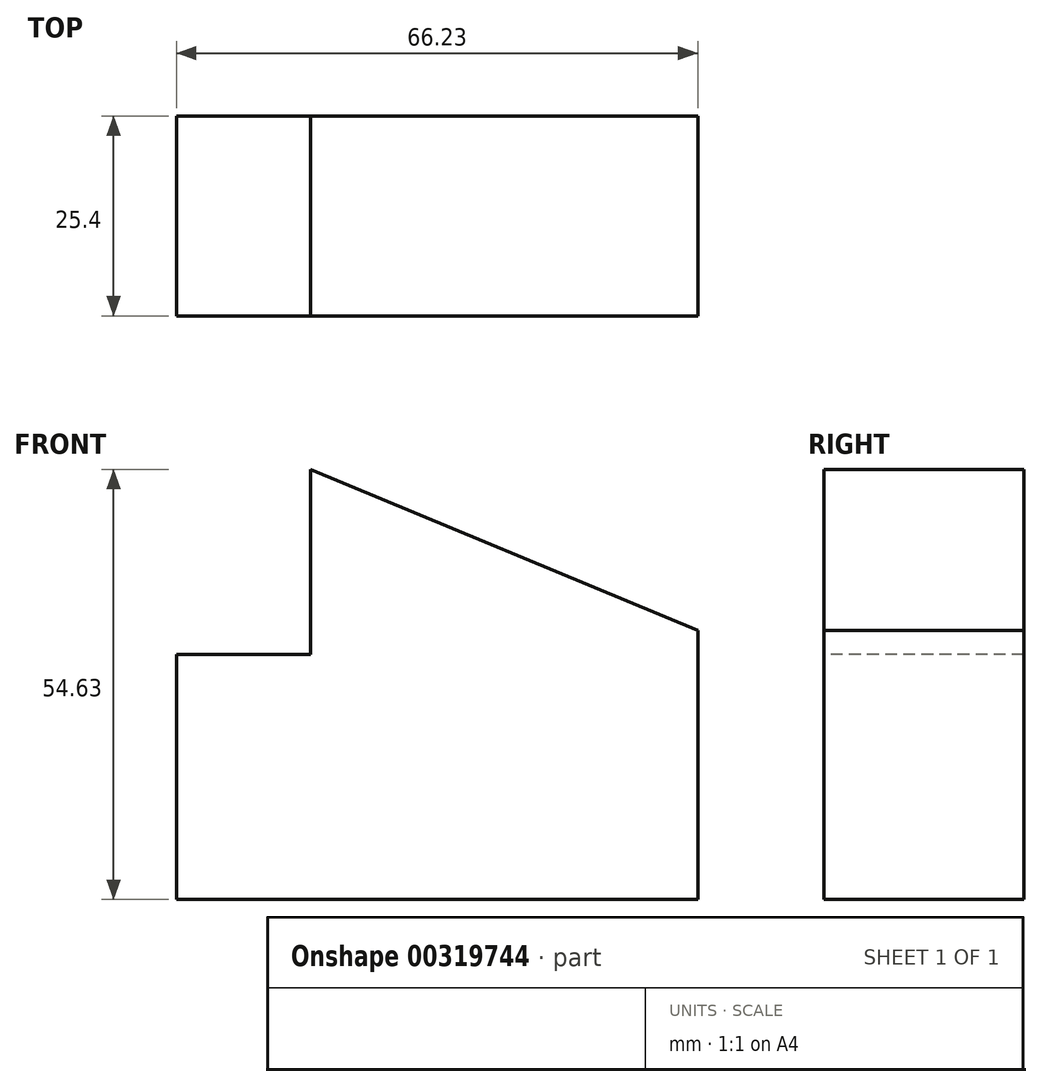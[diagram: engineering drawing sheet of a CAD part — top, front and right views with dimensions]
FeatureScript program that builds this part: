
annotation { "Feature Type Name" : "Feature", "Feature Type Description" : "" }
export const myFeature = defineFeature(function(context is Context, id is Id, definition is map)
    precondition{}
    {
        {
            var Q0;
            Q0=qCreatedBy(makeId("Front.planeOp"),FACE);
            var sketch = newSketch(context, id + "F0", { "sketchPlane" : qUnion([Q0])});
            skLineSegment(sketch, "E0", {"start": v(-19.5, 45.34) * mm, "end": v(-19.5, 31.1) * mm});
            skLineSegment(sketch, "E1", {"start": v(-19.5, 31.1) * mm, "end": v(-36.52, 31.1) * mm});
            skLineSegment(sketch, "E2", {"start": v(-36.52, 31.1) * mm, "end": v(-36.52, 0) * mm});
            skLineSegment(sketch, "E3", {"start": v(-36.52, 0) * mm, "end": v(29.71, 0) * mm});
            skLineSegment(sketch, "E4", {"start": v(29.71, 0) * mm, "end": v(29.71, 34.2) * mm});
            skLineSegment(sketch, "E5", {"start": v(29.71, 34.2) * mm, "end": v(-19.5, 54.63) * mm});
            skLineSegment(sketch, "E6", {"start": v(-19.5, 54.63) * mm, "end": v(-19.5, 45.34) * mm});
            skSolve(sketch);
        }
        {
            var Q0;
            Q0=makeQuery(id+"F0.imprint","IMPRINT",FACE,{"disambiguationData":[TD([[makeQuery(id+"F0.imprint","IMPRINT",EDGE,{"derivedFrom":sQuery(id+"F0.wireOp",EDGE,"E0")}),1.0]])]});
            extrude(context, id + "F1", {"entities" : qUnion([Q0]), "oppositeDirection" : true, "depth" : 25.4 * mm});
        }
    });
